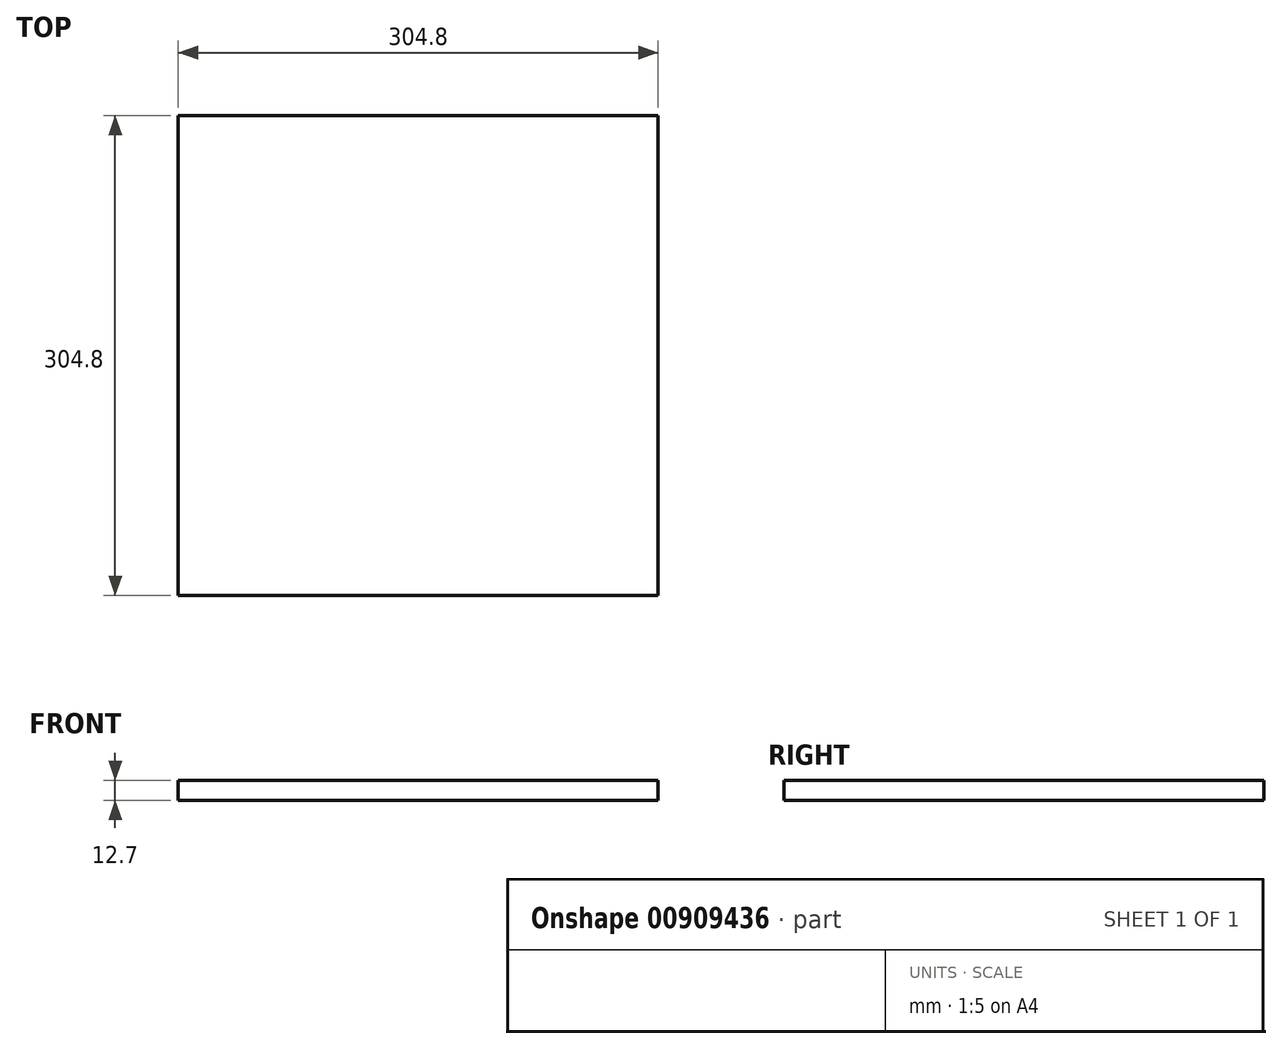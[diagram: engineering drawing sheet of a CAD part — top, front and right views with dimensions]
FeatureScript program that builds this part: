
annotation { "Feature Type Name" : "Feature", "Feature Type Description" : "" }
export const myFeature = defineFeature(function(context is Context, id is Id, definition is map)
    precondition{}
    {
        {
            var Q0;
            Q0=qCreatedBy(makeId("Top.planeOp"),FACE);
            var sketch = newSketch(context, id + "F0", { "sketchPlane" : qUnion([Q0])});
            skLineSegment(sketch, "E0.bottom", {"start": v(-152.4, 152.4) * mm, "end": v(152.4, 152.4) * mm});
            skLineSegment(sketch, "E0.top", {"start": v(-152.4, -152.4) * mm, "end": v(152.4, -152.4) * mm});
            skLineSegment(sketch, "E0.left", {"start": v(-152.4, 152.4) * mm, "end": v(-152.4, -152.4) * mm});
            skLineSegment(sketch, "E0.right", {"start": v(152.4, 152.4) * mm, "end": v(152.4, -152.4) * mm});
            skLineSegment(sketch, "E1", {"start": v(-152.4, 0) * mm, "end": v(0, 0) * mm, "construction": true});
            skLineSegment(sketch, "E2", {"start": v(0, 0) * mm, "end": v(0, 152.4) * mm, "construction": true});
            skSolve(sketch);
        }
        {
            var Q0;
            Q0=qSketchRegion(id+"F0",true);
            extrude(context, id + "F1", {"entities" : qUnion([Q0]), "depth" : 12.7 * mm, "offsetDistance" : 25.4 * mm});
        }
    });
